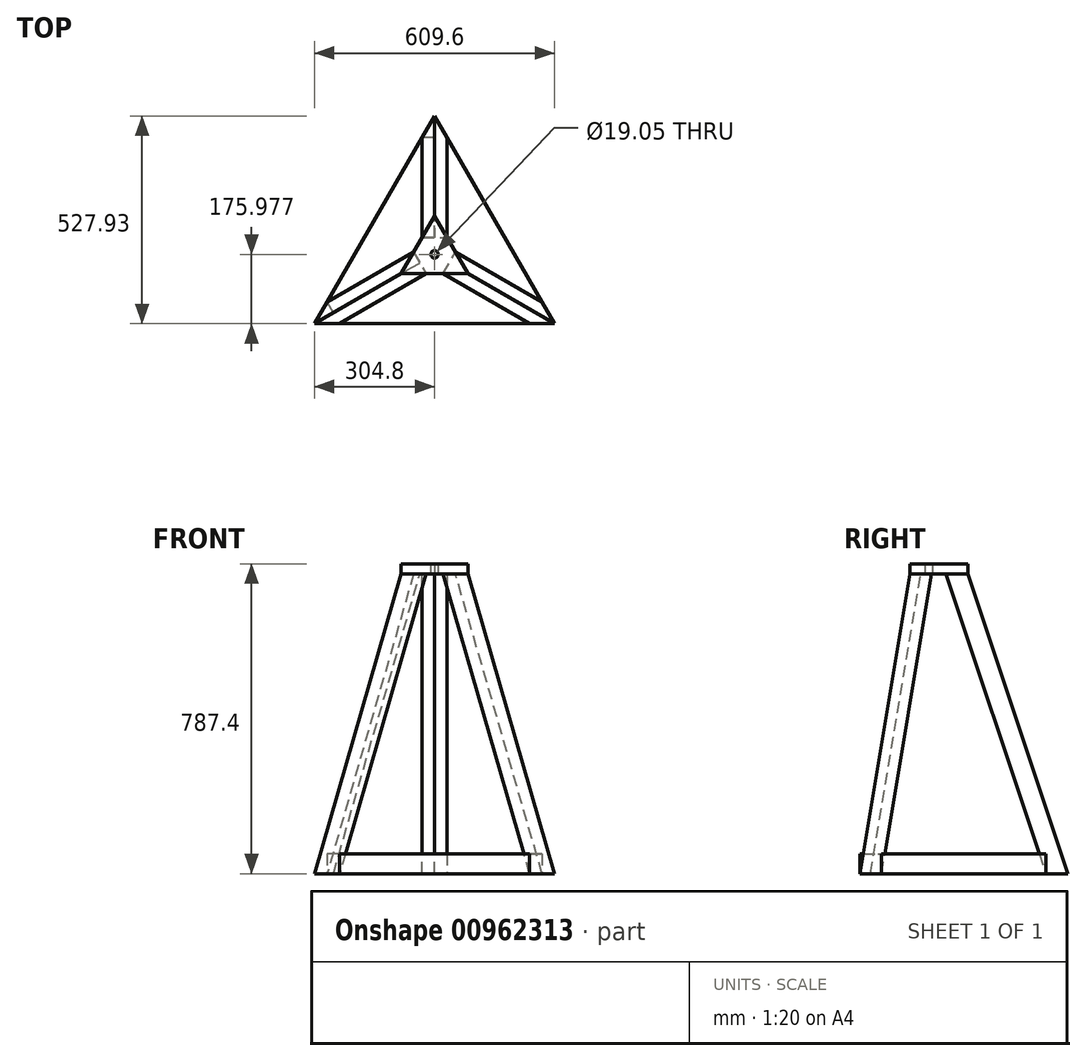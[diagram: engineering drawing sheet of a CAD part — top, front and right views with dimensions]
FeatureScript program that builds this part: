
annotation { "Feature Type Name" : "Feature", "Feature Type Description" : "" }
export const myFeature = defineFeature(function(context is Context, id is Id, definition is map)
    precondition{}
    {
        {
            var Q0;
            Q0=qCreatedBy(makeId("Top.planeOp"),FACE);
            var sketch = newSketch(context, id + "F0", { "sketchPlane" : qUnion([Q0])});
            skLineSegment(sketch, "E0", {"start": v(0, 0) * mm, "end": v(-304.8, -527.93) * mm});
            skLineSegment(sketch, "E1", {"start": v(-304.8, -527.93) * mm, "end": v(304.8, -527.93) * mm});
            skLineSegment(sketch, "E2", {"start": v(304.8, -527.93) * mm, "end": v(0, 0) * mm});
            skLineSegment(sketch, "E3", {"start": v(-304.8, -527.93) * mm, "end": v(-273.05, -472.94) * mm});
            skLineSegment(sketch, "E4", {"start": v(-304.8, -527.93) * mm, "end": v(-241.3, -527.93) * mm});
            skLineSegment(sketch, "E5", {"start": v(-241.3, -527.93) * mm, "end": v(-273.05, -472.94) * mm});
            skLineSegment(sketch, "E6.MirrorCS", {"start": v(241.3, -527.93) * mm, "end": v(273.05, -472.94) * mm});
            skLineSegment(sketch, "E7", {"start": v(0, 0) * mm, "end": v(-31.75, -55) * mm});
            skLineSegment(sketch, "E8", {"start": v(0, 0) * mm, "end": v(31.75, -55) * mm});
            skLineSegment(sketch, "E9", {"start": v(31.75, -55) * mm, "end": v(-31.75, -55) * mm});
            skLineSegment(sketch, "E10", {"start": v(-304.8, -527.93) * mm, "end": v(0, -351.95) * mm});
            skLineSegment(sketch, "E11", {"start": v(0, -351.95) * mm, "end": v(304.8, -527.93) * mm});
            skLineSegment(sketch, "E12", {"start": v(0, -351.95) * mm, "end": v(0, 0) * mm});
            skSolve(sketch);
        }
        {
            var Q0;
            {var subQ0=sQuery(id+"F0.wireOp",EDGE,"E9");var subQ1=sQuery(id+"F0.wireOp",EDGE,"E0");var subQ2=makeQuery(id+"F0.imprint","INTERSECT",VERTEX,{"derivedFrom":[subQ1,subQ0]});Q0=makeQuery(id+"F0.imprint","IMPRINT",FACE,{"disambiguationData":[TD([[makeQuery(id+"F0.imprint","IMPRINT",EDGE,{"disambiguationData":[TD([[subQ2,-1.0]])],"derivedFrom":subQ1}),1.0]])]});}
            cPlane(context, id + "F1", {"entities" : qUnion([Q0]), "cplaneType" : CPlaneType.OFFSET, "offset" : 762 * mm, "width" : 152.4 * mm, "height" : 152.4 * mm});
        }
        {
            var Q0;
            Q0=qCreatedBy(id+"F1.planeOp",FACE);
            var sketch = newSketch(context, id + "F2", { "sketchPlane" : qUnion([Q0])});
            skLineSegment(sketch, "E13.0.0", {"start": v(-304.8, -527.93) * mm, "end": v(304.8, -527.93) * mm});
            skLineSegment(sketch, "E13.0.1", {"start": v(304.8, -527.93) * mm, "end": v(0, 0) * mm});
            skLineSegment(sketch, "E13.0.2", {"start": v(0, 0) * mm, "end": v(-304.8, -527.93) * mm});
            skLineSegment(sketch, "E14", {"start": v(0, -254) * mm, "end": v(-84.83, -400.93) * mm});
            skLineSegment(sketch, "E15", {"start": v(84.83, -400.93) * mm, "end": v(0, -254) * mm});
            skLineSegment(sketch, "E16", {"start": v(84.83, -400.93) * mm, "end": v(-84.83, -400.93) * mm});
            skLineSegment(sketch, "E17", {"start": v(-84.83, -400.93) * mm, "end": v(-21.33, -400.93) * mm});
            skLineSegment(sketch, "E18", {"start": v(-84.83, -400.93) * mm, "end": v(-53.08, -345.94) * mm});
            skLineSegment(sketch, "E19", {"start": v(-53.08, -345.94) * mm, "end": v(-21.33, -400.93) * mm});
            skLineSegment(sketch, "E20.MirrorCS", {"start": v(53.08, -345.94) * mm, "end": v(21.33, -400.93) * mm});
            skLineSegment(sketch, "E21", {"start": v(0, -254) * mm, "end": v(-31.75, -309) * mm});
            skLineSegment(sketch, "E22", {"start": v(-31.75, -309) * mm, "end": v(31.75, -309) * mm});
            skLineSegment(sketch, "E23", {"start": v(31.75, -309) * mm, "end": v(0, -254) * mm});
            skSolve(sketch);
        }
        {
            var Q0;
            Q0=sQuery(id+"F2.wireOp",VERTEX,"E20.MirrorCS.end");
            var Q1;
            Q1=sQuery(id+"F2.wireOp",VERTEX,"E20.MirrorCS.start");
            var Q2;
            Q2=sQuery(id+"F0.wireOp",VERTEX,"E6.MirrorCS.start");
            cPlane(context, id + "F3", {"entities" : qUnion([Q0, Q1, Q2]), "cplaneType" : CPlaneType.THREE_POINT, "offset" : 25.4 * mm, "width" : 152.4 * mm, "height" : 152.4 * mm});
        }
        {
            var Q0;
            Q0=qCreatedBy(id+"F3.planeOp",FACE);
            var sketch = newSketch(context, id + "F4", { "sketchPlane" : qUnion([Q0])});
            skPoint(sketch, "E24.0", {"position": v(-213.68, 703.48) * mm});
            skPoint(sketch, "E25.0", {"position": v(-151.2, 692.07) * mm});
            skPoint(sketch, "E26.0", {"position": v(-357.94, -86.68) * mm});
            skPoint(sketch, "E27.0", {"position": v(-295.47, -98.08) * mm});
            skLineSegment(sketch, "E28", {"start": v(-213.68, 703.48) * mm, "end": v(-357.94, -86.68) * mm});
            skLineSegment(sketch, "E29", {"start": v(-151.2, 692.07) * mm, "end": v(-295.47, -98.08) * mm});
            skSolve(sketch);
        }
        {
            var Q0;
            Q0=qCreatedBy(id+"F3.planeOp",FACE);
            cPlane(context, id + "F5", {"entities" : qUnion([Q0]), "cplaneType" : CPlaneType.OFFSET, "offset" : 55 * mm, "width" : 152.4 * mm, "height" : 152.4 * mm});
        }
        {
            var Q0;
            {var subQ0=sQuery(id+"F2.wireOp",EDGE,"E20.MirrorCS");Q0=makeQuery(id+"F2.imprint","IMPRINT",FACE,{"disambiguationData":[TD([[makeQuery(id+"F2.imprint","IMPRINT",EDGE,{"derivedFrom":subQ0}),1.0]])]});}
            var Q1;
            {var subQ0=sQuery(id+"F0.wireOp",EDGE,"E11");var subQ1=sQuery(id+"F0.wireOp",EDGE,"E2");var subQ4=sQuery(id+"F0.wireOp",EDGE,"E6.MirrorCS");var subQ5=makeQuery(id+"F0.imprint","INTERSECT",VERTEX,{"derivedFrom":[subQ1,subQ4]});var subQ6=makeQuery(id+"F0.imprint","INTERSECT",VERTEX,{"derivedFrom":[subQ4,subQ0]});Q1=qUnion([makeQuery(id+"F0.imprint","IMPRINT",FACE,{"disambiguationData":[TD([[makeQuery(id+"F0.imprint","IMPRINT",EDGE,{"disambiguationData":[TD([[subQ6,1.0]])],"derivedFrom":subQ4}),-1.0]])]}),makeQuery(id+"F0.imprint","IMPRINT",FACE,{"disambiguationData":[TD([[makeQuery(id+"F0.imprint","IMPRINT",EDGE,{"disambiguationData":[TD([[subQ5,1.0]])],"derivedFrom":subQ4}),-1.0]])]})]);}
            var Q2;
            Q2=sQuery(id+"F4.wireOp",EDGE,"E28");
            sweep(context, id + "F6", {"profiles" : qUnion([Q0, Q1]), "path" : qUnion([Q2])});
        }
        {
            var Q0;
            Q0=sQuery(id+"F0.wireOp",EDGE,"E5");
            cPoint(context, id + "F7", {"entities" : qUnion([Q0]), "parameter" : 0.5});
        }
        {
            var Q0;
            Q0=sQuery(id+"F2.wireOp",VERTEX,"E18.end");
            var Q1;
            Q1=sQuery(id+"F2.wireOp",VERTEX,"E17.end");
            var Q2;
            Q2 = qCreatedBy(id + "F7" ,VERTEX);
            cPlane(context, id + "F8", {"entities" : qUnion([Q0, Q1, Q2]), "cplaneType" : CPlaneType.THREE_POINT, "offset" : 25.4 * mm, "width" : 152.4 * mm, "height" : 152.4 * mm});
        }
        {
            var Q0;
            Q0=qCreatedBy(id+"F8.planeOp",FACE);
            var sketch = newSketch(context, id + "F9", { "sketchPlane" : qUnion([Q0])});
            skPoint(sketch, "E30.0", {"position": v(151.2, 692.07) * mm});
            skPoint(sketch, "E31.0", {"position": v(213.68, 703.48) * mm});
            skPoint(sketch, "E32.0", {"position": v(295.47, -98.08) * mm});
            skPoint(sketch, "E33.0", {"position": v(357.94, -86.68) * mm});
            skLineSegment(sketch, "E34", {"start": v(357.94, -86.68) * mm, "end": v(213.68, 703.48) * mm});
            skLineSegment(sketch, "E35", {"start": v(295.47, -98.08) * mm, "end": v(151.2, 692.07) * mm});
            skSolve(sketch);
        }
        {
            var Q0;
            {var subQ1=sQuery(id+"F0.wireOp",EDGE,"E0");var subQ3=sQuery(id+"F0.wireOp",EDGE,"E5");var subQ4=makeQuery(id+"F0.imprint","INTERSECT",VERTEX,{"derivedFrom":[subQ1,subQ3]});Q0=makeQuery(id+"F0.imprint","IMPRINT",FACE,{"disambiguationData":[TD([[makeQuery(id+"F0.imprint","IMPRINT",EDGE,{"disambiguationData":[TD([[subQ4,1.0]])],"derivedFrom":subQ3}),1.0]])]});}
            var Q1;
            {var subQ0=sQuery(id+"F2.wireOp",EDGE,"E19");Q1=makeQuery(id+"F2.imprint","IMPRINT",FACE,{"disambiguationData":[TD([[makeQuery(id+"F2.imprint","IMPRINT",EDGE,{"derivedFrom":subQ0}),-1.0]])]});}
            var Q2;
            Q2=sQuery(id+"F9.wireOp",EDGE,"E34");
            sweep(context, id + "F10", {"profiles" : qUnion([Q0, Q1]), "path" : qUnion([Q2])});
        }
        {
            var Q0;
            Q0=sQuery(id+"F2.wireOp",VERTEX,"E21.end");
            var Q1;
            Q1=sQuery(id+"F2.wireOp",VERTEX,"E22.end");
            var Q2;
            Q2=sQuery(id+"F0.wireOp",VERTEX,"E8.end");
            cPlane(context, id + "F11", {"entities" : qUnion([Q0, Q1, Q2]), "cplaneType" : CPlaneType.THREE_POINT, "offset" : 25.4 * mm, "width" : 152.4 * mm, "height" : 152.4 * mm});
        }
        {
            var Q0;
            Q0=qCreatedBy(id+"F11.planeOp",FACE);
            var sketch = newSketch(context, id + "F12", { "sketchPlane" : qUnion([Q0])});
            skPoint(sketch, "E36.0", {"position": v(31.75, 820.6) * mm});
            skPoint(sketch, "E37.0", {"position": v(-31.75, 820.6) * mm});
            skPoint(sketch, "E38.0", {"position": v(31.75, 17.4) * mm});
            skPoint(sketch, "E39.0", {"position": v(-31.75, 17.4) * mm});
            skLineSegment(sketch, "E40", {"start": v(31.75, 820.6) * mm, "end": v(31.75, 17.4) * mm});
            skLineSegment(sketch, "E41", {"start": v(-31.75, 820.6) * mm, "end": v(-31.75, 17.4) * mm});
            skSolve(sketch);
        }
        {
            var Q0;
            {var subQ0=sQuery(id+"F2.wireOp",EDGE,"E22");Q0=makeQuery(id+"F2.imprint","IMPRINT",FACE,{"disambiguationData":[TD([[makeQuery(id+"F2.imprint","IMPRINT",EDGE,{"derivedFrom":subQ0}),1.0]])]});}
            var Q1;
            {var subQ0=sQuery(id+"F0.wireOp",EDGE,"E9");var subQ1=sQuery(id+"F0.wireOp",EDGE,"E0");var subQ2=makeQuery(id+"F0.imprint","INTERSECT",VERTEX,{"derivedFrom":[subQ1,subQ0]});Q1=makeQuery(id+"F0.imprint","IMPRINT",FACE,{"disambiguationData":[TD([[makeQuery(id+"F0.imprint","IMPRINT",EDGE,{"disambiguationData":[TD([[subQ2,1.0]])],"derivedFrom":subQ0}),-1.0]])]});}
            var Q2;
            Q2=sQuery(id+"F12.wireOp",EDGE,"E40");
            sweep(context, id + "F13", {"profiles" : qUnion([Q0, Q1]), "path" : qUnion([Q2])});
        }
        {
            var Q0;
            {var subQ1=sQuery(id+"F0.wireOp",EDGE,"E6.MirrorCS");var subQ5=sQuery(id+"F0.wireOp",EDGE,"E2");var subQ6=makeQuery(id+"F0.imprint","INTERSECT",VERTEX,{"derivedFrom":[subQ5,subQ1]});Q0=makeQuery(id+"F0.imprint","IMPRINT",FACE,{"disambiguationData":[TD([[makeQuery(id+"F0.imprint","IMPRINT",EDGE,{"disambiguationData":[TD([[subQ6,-1.0]])],"derivedFrom":subQ5}),1.0]])]});}
            var Q1;
            {var subQ0=sQuery(id+"F0.wireOp",EDGE,"E9");var subQ1=sQuery(id+"F0.wireOp",EDGE,"E0");var subQ2=makeQuery(id+"F0.imprint","INTERSECT",VERTEX,{"derivedFrom":[subQ1,subQ0]});Q1=makeQuery(id+"F0.imprint","IMPRINT",FACE,{"disambiguationData":[TD([[makeQuery(id+"F0.imprint","IMPRINT",EDGE,{"disambiguationData":[TD([[subQ2,-1.0]])],"derivedFrom":subQ1}),1.0]])]});}
            var Q2;
            {var subQ1=sQuery(id+"F0.wireOp",EDGE,"E5");var subQ7=sQuery(id+"F0.wireOp",EDGE,"E1");var subQ9=makeQuery(id+"F0.imprint","INTERSECT",VERTEX,{"derivedFrom":[subQ7,subQ1]});Q2=makeQuery(id+"F0.imprint","IMPRINT",FACE,{"disambiguationData":[TD([[makeQuery(id+"F0.imprint","IMPRINT",EDGE,{"disambiguationData":[TD([[subQ9,-1.0]])],"derivedFrom":subQ7}),1.0]])]});}
            extrude(context, id + "F14", {"entities" : qUnion([Q0, Q1, Q2]), "depth" : 50.8 * mm, "offsetDistance" : 25.4 * mm});
        }
        {
            var Q0;
            {var subQ0=sQuery(id+"F2.wireOp",EDGE,"E22");Q0=makeQuery(id+"F2.imprint","IMPRINT",FACE,{"disambiguationData":[TD([[makeQuery(id+"F2.imprint","IMPRINT",EDGE,{"derivedFrom":subQ0}),1.0]])]});}
            var Q1;
            {var subQ0=sQuery(id+"F2.wireOp",EDGE,"E19");Q1=makeQuery(id+"F2.imprint","IMPRINT",FACE,{"disambiguationData":[TD([[makeQuery(id+"F2.imprint","IMPRINT",EDGE,{"derivedFrom":subQ0}),-1.0]])]});}
            var Q2;
            {var subQ0=sQuery(id+"F2.wireOp",EDGE,"E20.MirrorCS");Q2=makeQuery(id+"F2.imprint","IMPRINT",FACE,{"disambiguationData":[TD([[makeQuery(id+"F2.imprint","IMPRINT",EDGE,{"derivedFrom":subQ0}),1.0]])]});}
            var Q3;
            {var subQ0=sQuery(id+"F2.wireOp",EDGE,"E19");Q3=makeQuery(id+"F2.imprint","IMPRINT",FACE,{"disambiguationData":[TD([[makeQuery(id+"F2.imprint","IMPRINT",EDGE,{"derivedFrom":subQ0}),1.0]])]});}
            extrude(context, id + "F15", {"entities" : qUnion([Q0, Q1, Q2, Q3]), "depth" : 25.4 * mm, "offsetDistance" : 25.4 * mm});
        }
        {
            var Q0;
            Q0=makeQuery(id+"F15.opExtrude","CAP_FACE",FACE,{"disambiguationData":[OSD([sQuery(id+"F2.wireOp",EDGE,"E14"),sQuery(id+"F2.wireOp",EDGE,"E15"),sQuery(id+"F2.wireOp",EDGE,"E16")])],"isStart":false});
            var sketch = newSketch(context, id + "F16", { "sketchPlane" : qUnion([Q0])});
            skPoint(sketch, "E42.0", {"position": v(0, -351.95) * mm});
            skCircle(sketch, "E43", {"center": v(0, -351.95) * mm, "radius": 9.53 * mm});
            skSolve(sketch);
        }
        {
            var Q0;
            Q0=makeQuery(id+"F16.imprint","IMPRINT",FACE,{"disambiguationData":[TD([[makeQuery(id+"F16.imprint","IMPRINT",EDGE,{"derivedFrom":sQuery(id+"F16.wireOp",EDGE,"E43")}),1.0]])]});
            extrude(context, id + "F17", {"entities" : qUnion([Q0]), "operationType" : NewBodyOperationType.REMOVE, "oppositeDirection" : true, "depth" : 25.4 * mm, "offsetDistance" : 25.4 * mm});
        }
    });
